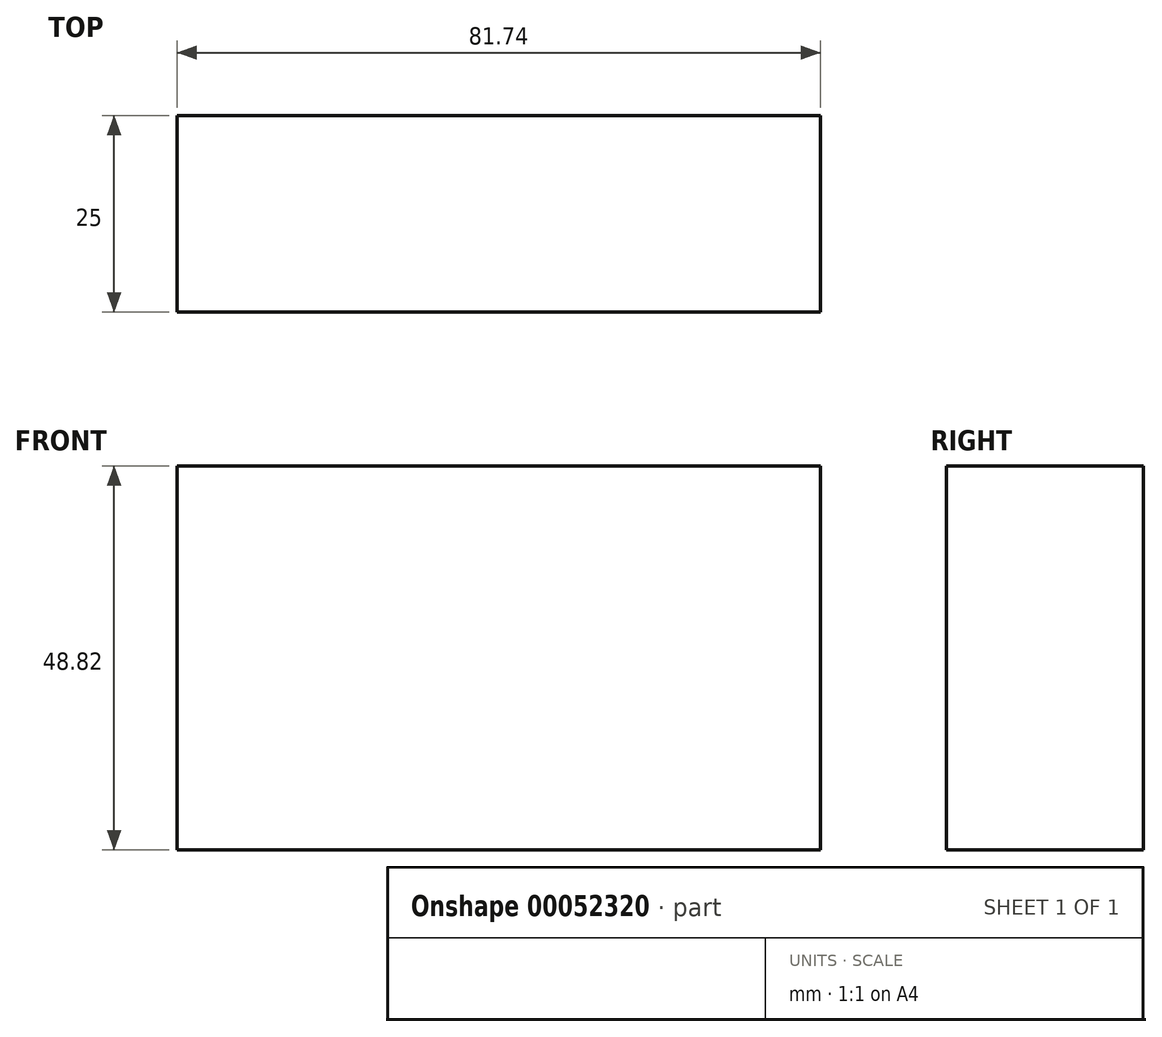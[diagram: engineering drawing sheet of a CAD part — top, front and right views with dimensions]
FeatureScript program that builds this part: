
annotation { "Feature Type Name" : "Feature", "Feature Type Description" : "" }
export const myFeature = defineFeature(function(context is Context, id is Id, definition is map)
    precondition{}
    {
        {
            var Q0;
            Q0=qCreatedBy(makeId("Front.planeOp"),FACE);
            var sketch = newSketch(context, id + "F0", { "sketchPlane" : qUnion([Q0])});
            skLineSegment(sketch, "E0.rect.bottom", {"start": v(40.87, 24.4) * mm, "end": v(-40.87, 24.4) * mm});
            skLineSegment(sketch, "E0.rect.top", {"start": v(40.87, -24.4) * mm, "end": v(-40.87, -24.4) * mm});
            skLineSegment(sketch, "E0.rect.left", {"start": v(40.87, 24.4) * mm, "end": v(40.87, -24.4) * mm});
            skLineSegment(sketch, "E0.rect.right", {"start": v(-40.87, 24.4) * mm, "end": v(-40.87, -24.4) * mm});
            skPoint(sketch, "E0.rect.middle", {"position": v(0, 0) * mm});
            skSolve(sketch);
        }
        {
            var Q0;
            Q0 = qSketchRegion(id + "F0", true);
            extrude(context, id + "F1", {"entities" : qUnion([Q0]), "depth" : 25 * mm});
        }
    });
